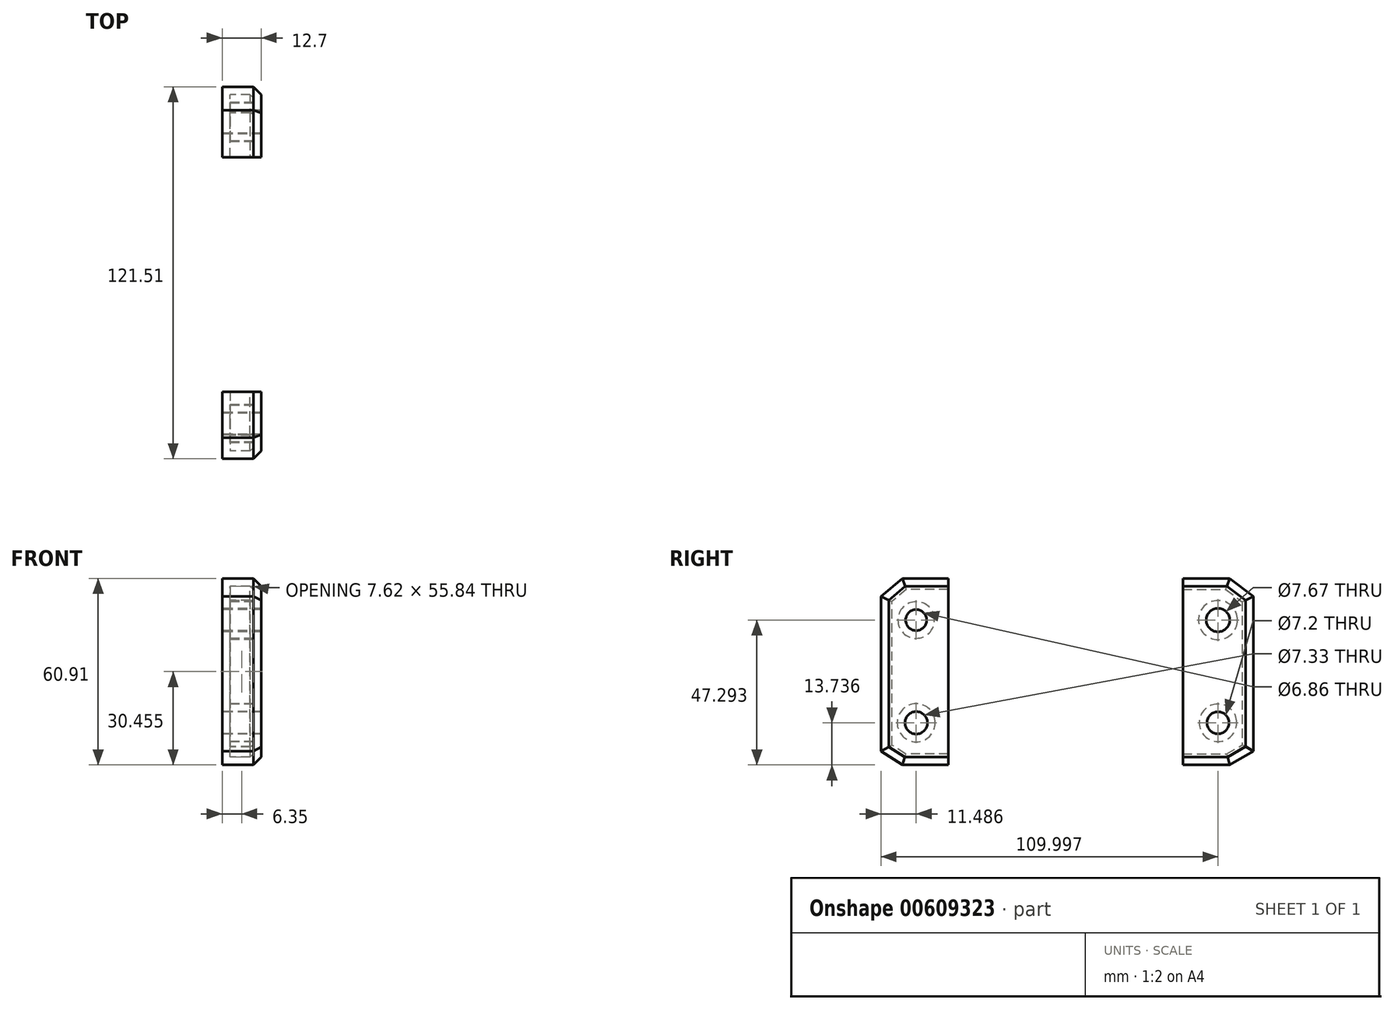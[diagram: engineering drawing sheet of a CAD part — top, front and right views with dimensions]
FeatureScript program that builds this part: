
annotation { "Feature Type Name" : "Feature", "Feature Type Description" : "" }
export const myFeature = defineFeature(function(context is Context, id is Id, definition is map)
    precondition{}
    {
        {
            var Q0;
            Q0=qCreatedBy(makeId("Right.planeOp"),FACE);
            var sketch = newSketch(context, id + "F0", { "sketchPlane" : qUnion([Q0])});
            skLineSegment(sketch, "E0", {"start": v(33.08, 31.65) * mm, "end": v(48.35, 31.65) * mm});
            skLineSegment(sketch, "E1", {"start": v(33.08, -29.26) * mm, "end": v(48.35, -29.26) * mm});
            skLineSegment(sketch, "E2", {"start": v(-43.51, 31.65) * mm, "end": v(-58.5, 31.65) * mm});
            skLineSegment(sketch, "E3", {"start": v(-43.51, -29.26) * mm, "end": v(-58.5, -29.26) * mm});
            skLineSegment(sketch, "E4", {"start": v(-43.51, 31.65) * mm, "end": v(-43.51, -29.26) * mm});
            skLineSegment(sketch, "E5", {"start": v(33.08, -29.26) * mm, "end": v(33.08, 31.65) * mm});
            skLineSegment(sketch, "E6", {"start": v(-58.5, 31.65) * mm, "end": v(-65.46, 25.7) * mm});
            skLineSegment(sketch, "E7", {"start": v(-58.5, -29.26) * mm, "end": v(-65.46, -24.8) * mm});
            skLineSegment(sketch, "E8", {"start": v(-65.46, -24.8) * mm, "end": v(-65.46, 25.7) * mm});
            skLineSegment(sketch, "E9", {"start": v(48.35, 31.65) * mm, "end": v(56.05, 25.7) * mm});
            skLineSegment(sketch, "E10", {"start": v(48.35, -29.26) * mm, "end": v(56.05, -24.8) * mm});
            skLineSegment(sketch, "E11", {"start": v(56.05, 25.7) * mm, "end": v(56.05, -24.8) * mm});
            skCircle(sketch, "E12", {"center": v(44.54, 18.03) * mm, "radius": 3.84 * mm});
            skCircle(sketch, "E13", {"center": v(44.54, -15.52) * mm, "radius": 3.6 * mm});
            skCircle(sketch, "E14", {"center": v(-53.97, 18.03) * mm, "radius": 3.43 * mm});
            skCircle(sketch, "E15", {"center": v(-53.97, -15.52) * mm, "radius": 3.66 * mm});
            skCircle(sketch, "E16", {"center": v(44.54, 18.03) * mm, "radius": 4.03 * mm, "construction": true});
            skSolve(sketch);
        }
        {
            var Q0;
            Q0 = qSketchRegion(id + "F0", true);
            extrude(context, id + "F1", {"entities" : qUnion([Q0]), "depth" : 12.7 * mm, "offsetDistance" : 25.4 * mm});
        }
        {
            var Q0;
            Q0=makeQuery(id+"F1.opExtrude","CAP_EDGE",EDGE,{"disambiguationData":[OSD([sQuery(id+"F0.wireOp",EDGE,"E0")])],"isStart":false});
            var Q1;
            Q1=makeQuery(id+"F1.opExtrude","CAP_EDGE",EDGE,{"disambiguationData":[OSD([sQuery(id+"F0.wireOp",EDGE,"E9")])],"isStart":false});
            var Q2;
            Q2=makeQuery(id+"F1.opExtrude","CAP_EDGE",EDGE,{"disambiguationData":[OSD([sQuery(id+"F0.wireOp",EDGE,"E11")])],"isStart":false});
            var Q3;
            Q3=makeQuery(id+"F1.opExtrude","CAP_EDGE",EDGE,{"disambiguationData":[OSD([sQuery(id+"F0.wireOp",EDGE,"E1")])],"isStart":false});
            var Q4;
            Q4=makeQuery(id+"F1.opExtrude","CAP_EDGE",EDGE,{"disambiguationData":[OSD([sQuery(id+"F0.wireOp",EDGE,"E10")])],"isStart":false});
            var Q5;
            Q5=makeQuery(id+"F1.opExtrude","CAP_EDGE",EDGE,{"disambiguationData":[OSD([sQuery(id+"F0.wireOp",EDGE,"E2")])],"isStart":false});
            var Q6;
            Q6=makeQuery(id+"F1.opExtrude","CAP_EDGE",EDGE,{"disambiguationData":[OSD([sQuery(id+"F0.wireOp",EDGE,"E6")])],"isStart":false});
            var Q7;
            Q7=makeQuery(id+"F1.opExtrude","CAP_EDGE",EDGE,{"disambiguationData":[OSD([sQuery(id+"F0.wireOp",EDGE,"E8")])],"isStart":false});
            var Q8;
            Q8=makeQuery(id+"F1.opExtrude","CAP_EDGE",EDGE,{"disambiguationData":[OSD([sQuery(id+"F0.wireOp",EDGE,"E7")])],"isStart":false});
            var Q9;
            Q9=makeQuery(id+"F1.opExtrude","CAP_EDGE",EDGE,{"disambiguationData":[OSD([sQuery(id+"F0.wireOp",EDGE,"E3")])],"isStart":false});
            chamfer(context, id + "F2", {"entities" : qUnion([Q0, Q1, Q2, Q3, Q4, Q5, Q6, Q7, Q8, Q9]), "width" : 2.54 * mm, "tangentPropagation" : true});
        }
        {
            var Q0;
            Q0=makeQuery(id+"F1.opExtrude","SWEPT_FACE",FACE,{"disambiguationData":[OSD([sQuery(id+"F0.wireOp",EDGE,"E5")])]});
            var Q1;
            Q1=makeQuery(id+"F1.opExtrude","SWEPT_FACE",FACE,{"disambiguationData":[OSD([sQuery(id+"F0.wireOp",EDGE,"E4")])]});
            shell(context, id + "F3", {"entities" : qUnion([Q0, Q1]), "thickness" : 2.54 * mm});
        }
    });
